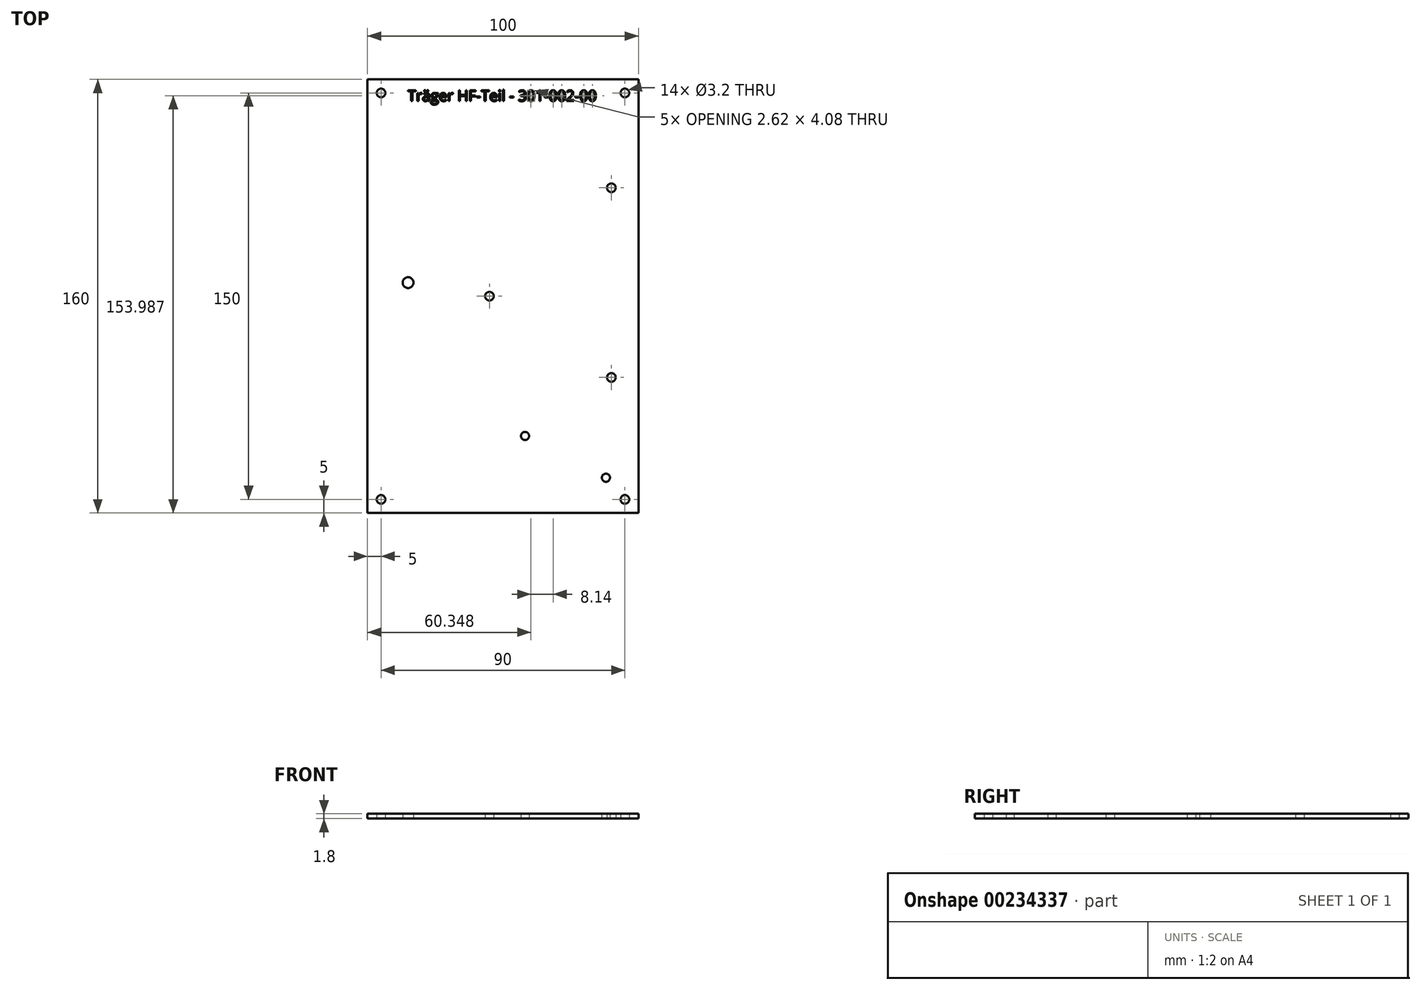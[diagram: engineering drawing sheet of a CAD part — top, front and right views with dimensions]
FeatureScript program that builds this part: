
annotation { "Feature Type Name" : "Feature", "Feature Type Description" : "" }
export const myFeature = defineFeature(function(context is Context, id is Id, definition is map)
    precondition{}
    {
        {
            var Q0;
            Q0=qCreatedBy(makeId("Top.planeOp"),FACE);
            var sketch = newSketch(context, id + "F0", { "sketchPlane" : qUnion([Q0])});
            skLineSegment(sketch, "E0.bottom", {"start": v(50, -80) * mm, "end": v(-50, -80) * mm});
            skLineSegment(sketch, "E0.top", {"start": v(50, 80) * mm, "end": v(-50, 80) * mm});
            skLineSegment(sketch, "E0.left", {"start": v(50, -80) * mm, "end": v(50, 80) * mm});
            skLineSegment(sketch, "E0.right", {"start": v(-50, -80) * mm, "end": v(-50, 80) * mm});
            skPoint(sketch, "E0.middle", {"position": v(0, 0) * mm});
            skCircle(sketch, "E1", {"center": v(-45, 75) * mm, "radius": 1.6 * mm});
            skCircle(sketch, "E2", {"center": v(45, 75) * mm, "radius": 1.6 * mm});
            skCircle(sketch, "E3", {"center": v(-45, -75) * mm, "radius": 1.6 * mm});
            skCircle(sketch, "E4", {"center": v(45, -75) * mm, "radius": 1.6 * mm});
            skLineSegment(sketch, "E5", {"start": v(0, 80) * mm, "end": v(0, -80) * mm, "construction": true});
            skPoint(sketch, "E5.startSnap0", {"position": v(0, 80) * mm});
            skLineSegment(sketch, "E6", {"start": v(-50, 0) * mm, "end": v(50, 0) * mm, "construction": true});
            skCircle(sketch, "E7", {"center": v(-35, 5) * mm, "radius": 2 * mm});
            skCircle(sketch, "E8", {"center": v(-5, 0) * mm, "radius": 1.6 * mm});
            skLineSegment(sketch, "E9", {"start": v(-35, 22.87) * mm, "end": v(-35, -75) * mm, "construction": true});
            skLineSegment(sketch, "E10", {"start": v(-5, 0) * mm, "end": v(-5, -75) * mm, "construction": true});
            skCircle(sketch, "E11", {"center": v(40, -30) * mm, "radius": 1.6 * mm});
            skCircle(sketch, "E12", {"center": v(40, 40) * mm, "radius": 1.6 * mm});
            skLineSegment(sketch, "E13.bottom", {"start": v(45, -70) * mm, "end": v(1.15, -70) * mm, "construction": true});
            skLineSegment(sketch, "E13.top", {"start": v(45, -48.57) * mm, "end": v(1.15, -48.57) * mm, "construction": true});
            skLineSegment(sketch, "E13.left", {"start": v(45, -70) * mm, "end": v(45, -48.57) * mm, "construction": true});
            skLineSegment(sketch, "E13.right", {"start": v(1.15, -70) * mm, "end": v(1.15, -48.57) * mm, "construction": true});
            skPoint(sketch, "E13.middle", {"position": v(23.07, -59.28) * mm});
            skCircle(sketch, "E14", {"center": v(8.15, -51.57) * mm, "radius": 1.5 * mm});
            skCircle(sketch, "E15", {"center": v(38, -67) * mm, "radius": 1.5 * mm});
            skSolve(sketch);
        }
        {
            var Q0;
            Q0=makeQuery(id+"F0.imprint","IMPRINT",FACE,{"disambiguationData":[TD([[makeQuery(id+"F0.imprint","IMPRINT",EDGE,{"derivedFrom":sQuery(id+"F0.wireOp",EDGE,"E0.bottom")}),-1.0]])]});
            extrude(context, id + "F1", {"entities" : qUnion([Q0]), "depth" : 1.8 * mm});
        }
        {
            var Q0;
            Q0=makeQuery(id+"F1.opExtrude","CAP_FACE",FACE,{"disambiguationData":[OSD([sQuery(id+"F0.wireOp",EDGE,"E0.bottom"),sQuery(id+"F0.wireOp",EDGE,"E0.top"),sQuery(id+"F0.wireOp",EDGE,"E0.left"),sQuery(id+"F0.wireOp",EDGE,"E0.right"),sQuery(id+"F0.wireOp",EDGE,"E1"),sQuery(id+"F0.wireOp",EDGE,"E2"),sQuery(id+"F0.wireOp",EDGE,"E3"),sQuery(id+"F0.wireOp",EDGE,"E4"),sQuery(id+"F0.wireOp",EDGE,"E7"),sQuery(id+"F0.wireOp",EDGE,"E8"),sQuery(id+"F0.wireOp",EDGE,"E11"),sQuery(id+"F0.wireOp",EDGE,"E12")])],"isStart":false});
            var sketch = newSketch(context, id + "F2", { "sketchPlane" : qUnion([Q0])});
            skText(sketch, "E16", { "text": "Träger HF-Teil - 301-002-00", "fontName": "OpenSans-Regular.ttf"});
            const initialGuessF2  = {"E16": [-0.03515, 0.072, 1, 0, 0.004]};
            skSetInitialGuess(sketch, initialGuessF2);
            skSolve(sketch);
        }
        {
            var Q0;
            Q0 = qSketchRegion(id + "F2", true);
            extrude(context, id + "F3", {"entities" : qUnion([Q0]), "operationType" : NewBodyOperationType.REMOVE, "oppositeDirection" : true, "depth" : .1 * mm});
        }
    });
